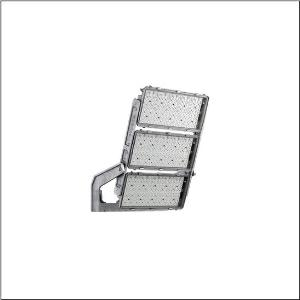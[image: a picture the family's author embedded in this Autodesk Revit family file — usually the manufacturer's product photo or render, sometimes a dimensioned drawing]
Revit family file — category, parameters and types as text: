
# Revit family: floodlight_fl_11_maxi_pro_remote___pl43_5xa779427a01aa_51b3
name_source: partatom
category: Lighting Fixtures
units: mm (PartAtom-declared; Revit-internal decimal feet)

## family parameters
Cut with Voids When Loaded = No
Host = Face
Light Source = No
Part Type = Normal
Room Calculation Point = No
Round Connector Dimension = Use Diameter
Shared = No

## types (1)
- --- (1 x LED, 177380 lm, 1425.5 W, 5000K)
    Apparent Load = 1425 VA
    CIE Flux Codes = 25 74 99 100 100
    Color Rendering = 70
    Color Temperature = 5000K
    Default Elevation = 1800 mm
    Description = Floodlight FL 11  maxi  pro Remote floodlight; light control with lens of PMMA; cover panel of toughened safety glass, transparent; light distribution: PL43, asymmetric direct distribution, LEDcolour temperature: 5000K, rated luminous flux: 177.380lm, colour rendering: CRI > 70, light colour: 750; luminous efficacy: 124lm/W; brightness control: DALI 2 (1 DALI address); with terminal, 8-pole, max. 2.5mm², mains connection: 220..240V/380..400V AC, 50/60Hz, surge voltage resistance: line to ground: 10kV, ECG replaceable separately, LED unit replaceable without ESD environment, dustproof LED module, dimming range 10..100%, no afterglow with DALI off / DMX off command; 1426W floodlight with 2x LED unit of diecast aluminium, coated grey; length: 713mm / width: 651mm / height: 338mm; mounting bracket, of diecast aluminium, uncoated, natural, equipment: Power, protection rating (complete): IP66; insulation class (complete): insulation class I (protective earthing); certification: CE, ENEC, VDE; ball protection: ball impact resistance with accessories, impact resistance: IK07; rated ambient temperature 10°C, only for outdoor installations, permissible operating ambient temperature: -40..+30°C, permissible storage temperature: -40..+85°C; packaging unit: 1 piece

Light Distribution: PL43
    Height = 320 mm
    Lamp = 1 x LED
    Lamp Light Flux = 177380 lm
    Lamp Power = 1425.5 W
    Lamp count = 1
    Length = 1002 mm
    Luminous efficacy = 124 lm/W
    Manufacturer = Siteco
    ModVariant = No
    Model = 5XA779427A01AA
    Mounting Place = Ceiling
    Mounting Type = Surface mounted
    Number of Poles = 1
    OnlyDefault = Yes
    Power Factor = 1
    Product Name = Floodlight FL 11 maxi pro Remote | PL43
    Product group = floodlight | ceiling mounted
    ProductGroupID = 302
    Protection Class = Protection class I
    Protection Degree = IP 66
    RLX_Detail_Level = 1
    RLX_Emergency_Light_Flux = 0 lm
    RLX_Emergency_Type = 0
    RLX_Emergency_Type_DB = No
    RlxData = <blob elided: 52465 chars, md5=393a64fb>
    Socket = socket
    Standby Power = 0 W
    System Light Flux = 177380 lm
    System Power = 1425 W
    Type Comments = factory setting: luminous flux: 100 % | dim-lin: 254 | 980 mA
    Type Image = l_1006784.jpg
    URL = http://relux.com
    VarID = @adj_065275
    Voltage = 0 V
    Weight = 0.00 kg
    Width = 655 mm

## geometry (parser evidence)
native form markers: Blend x4, Sweep x14
no freeform markers — native parametric forms only
